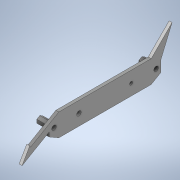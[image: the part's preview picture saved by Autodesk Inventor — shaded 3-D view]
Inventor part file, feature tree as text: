
AUTODESK INVENTOR PART (.ipt)
format: ipt  version: 2020 (Build 240168000, 168)  size: 175,104 bytes
history: native  units: in
note: dims shown in document units (in); Inventor stores cm internally (conversion verified against a paired STEP export)
features: other x3, extrude x2, sketch x2
ambient origin geometry x8: Origin, YZ Plane, XZ Plane, XY Plane, X Axis, Y Axis, Z Axis, Center Point
bodies: Solid1 (feature_tree)
feature tree (7):
  other  "HexWheelGuard.ipt"
  extrude  "Extrusion1"  Depth=0.315in
  extrude  "Extrusion2"  Depth=0.3937in
  other  "Solid1::HexWheelGuard.ipt"
  other  "TaggingFeature2"
  sketch  "Sketch1"  dims[d1=0.3937in d2=0.315in]
  sketch  "Sketch2"  dims[d3=60.0deg d4=1.4843in d5=0.0787in d6=0.3937in d7=0.0in d10=0.5906in d11=1.1024in d12=0.3937in d13=0.0in]
